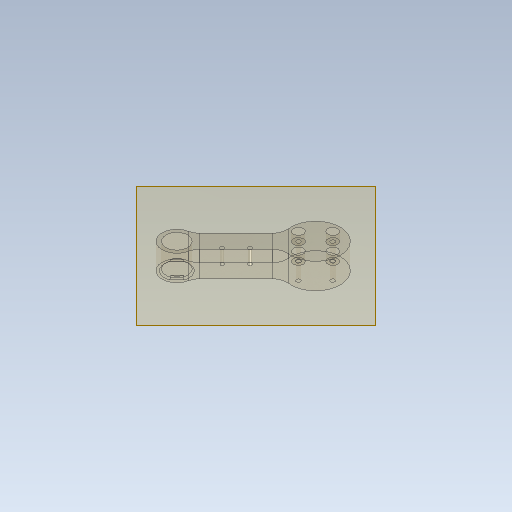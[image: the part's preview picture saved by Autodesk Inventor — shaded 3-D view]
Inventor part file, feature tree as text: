
AUTODESK INVENTOR PART (.ipt)
format: ipt  version: 2024.2 (Build 282272000, 272)  size: 150,528 bytes
history: native  units: in
note: dims shown in document units (in); Inventor stores cm internally (conversion verified against a paired STEP export)
features: other x4, plane x1
ambient origin geometry x8: Origin, YZ Plane, XZ Plane, XY Plane, X Axis, Y Axis, Z Axis, Center Point
bodies: Body1 (feature_tree)
feature tree (5):
  other  "5 Barras Version 0.ipt"
  plane  "Work Plane1"
  other  "Proximal Link 1::5 Barras Version 0.ipt"
  other  "TaggingFeature1"
  other  "Proximal Link 1"
